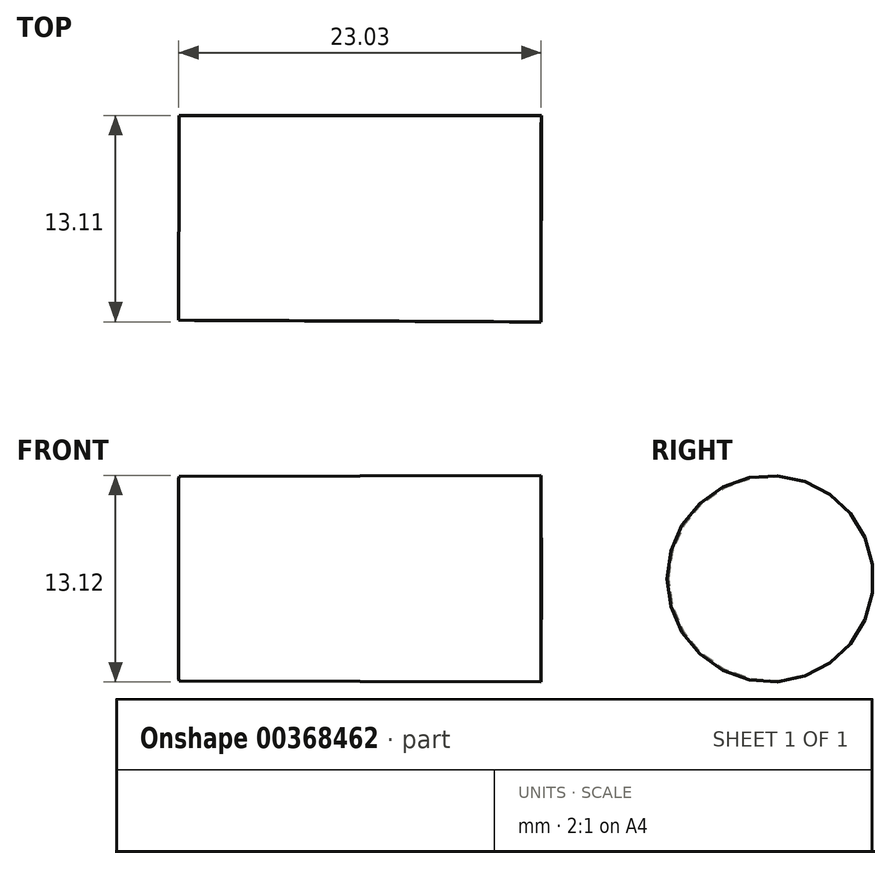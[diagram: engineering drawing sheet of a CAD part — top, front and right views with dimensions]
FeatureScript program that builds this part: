
annotation { "Feature Type Name" : "Feature", "Feature Type Description" : "" }
export const myFeature = defineFeature(function(context is Context, id is Id, definition is map)
    precondition{}
    {
        {
            var Q0;
            Q0=qCreatedBy(makeId("Top.planeOp"),FACE);
            var sketch = newSketch(context, id + "F0", { "sketchPlane" : qUnion([Q0])});
            skPoint(sketch, "E0", {"position": v(29, 0) * mm});
            skPoint(sketch, "E1", {"position": v(-38, 0) * mm});
            skLineSegment(sketch, "E2", {"start": v(-60.97, -10) * mm, "end": v(-60.97, 10) * mm});
            skPoint(sketch, "E3", {"position": v(-60.97, 6.5) * mm});
            skPoint(sketch, "E4", {"position": v(-60.97, -6.5) * mm});
            skLineSegment(sketch, "E5", {"start": v(-60.97, 6.5) * mm, "end": v(-83.97, 6.5) * mm});
            skLineSegment(sketch, "E6", {"start": v(-83.97, 6.5) * mm, "end": v(-84, -6.5) * mm});
            skLineSegment(sketch, "E7", {"start": v(-84, -6.5) * mm, "end": v(-60.97, -6.5) * mm});
            skArc(sketch, "E8", {"start": v(-23.54, -12.56) * mm, "mid": v(-35.77, -9.23) * mm, "end": v(-48.41, -10.1) * mm});
            skArc(sketch, "E9", {"start": v(-48.41, 10.1) * mm, "mid": v(-48.38, 10.05) * mm, "end": v(-48.35, 10) * mm});
            skArc(sketch, "E10.MirrorC", {"start": v(-23.54, 12.56) * mm, "mid": v(-35.6, 9.25) * mm, "end": v(-48.1, 10.03) * mm});
            skArc(sketch, "E11.MirrorC", {"start": v(-48.41, -10.1) * mm, "mid": v(-48.38, -10.05) * mm, "end": v(-48.35, -10) * mm});
            skArc(sketch, "E12.trimOffspring", {"start": v(-23.54, 12.56) * mm, "mid": v(6, 17.43) * mm, "end": v(33.83, 6.37) * mm});
            skArc(sketch, "E13.trimOffspring", {"start": v(-23.54, -12.56) * mm, "mid": v(6, -17.43) * mm, "end": v(33.83, -6.37) * mm});
            skArc(sketch, "E14", {"start": v(33.83, -6.37) * mm, "mid": v(37, 0) * mm, "end": v(33.83, 6.37) * mm});
            skLineSegment(sketch, "E15", {"start": v(-60.97, 10) * mm, "end": v(-60.97, -10) * mm});
            skPoint(sketch, "E16", {"position": v(-60.97, 0) * mm});
            skLineSegment(sketch, "E17", {"start": v(-60.97, 10) * mm, "end": v(-47.97, 10) * mm});
            skLineSegment(sketch, "E18", {"start": v(-60.97, -10) * mm, "end": v(-47.97, -10) * mm});
            skLineSegment(sketch, "E19", {"start": v(-83.98, 0) * mm, "end": v(37, -0.3) * mm});
            skSolve(sketch);
        }
        {
            var Q0;
            {var subQ0=sQuery(id+"F0.wireOp",EDGE,"E5");Q0=makeQuery(id+"F0.imprint","IMPRINT",FACE,{"disambiguationData":[TD([[makeQuery(id+"F0.imprint","IMPRINT",EDGE,{"derivedFrom":subQ0}),1.0]])]});}
            var Q1;
            {var subQ8=sQuery(id+"F0.wireOp",EDGE,"E12.trimOffspring");Q1=makeQuery(id+"F0.imprint","IMPRINT",FACE,{"disambiguationData":[TD([[makeQuery(id+"F0.imprint","IMPRINT",EDGE,{"derivedFrom":subQ8}),-1.0]])]});}
            var Q2;
            Q2=sQuery(id+"F0.wireOp",EDGE,"E19");
            revolve(context, id + "F1", {"entities" : qUnion([Q0, Q1]), "axis" : qUnion([Q2]), "revolveType" : RevolveType.FULL});
        }
    });
